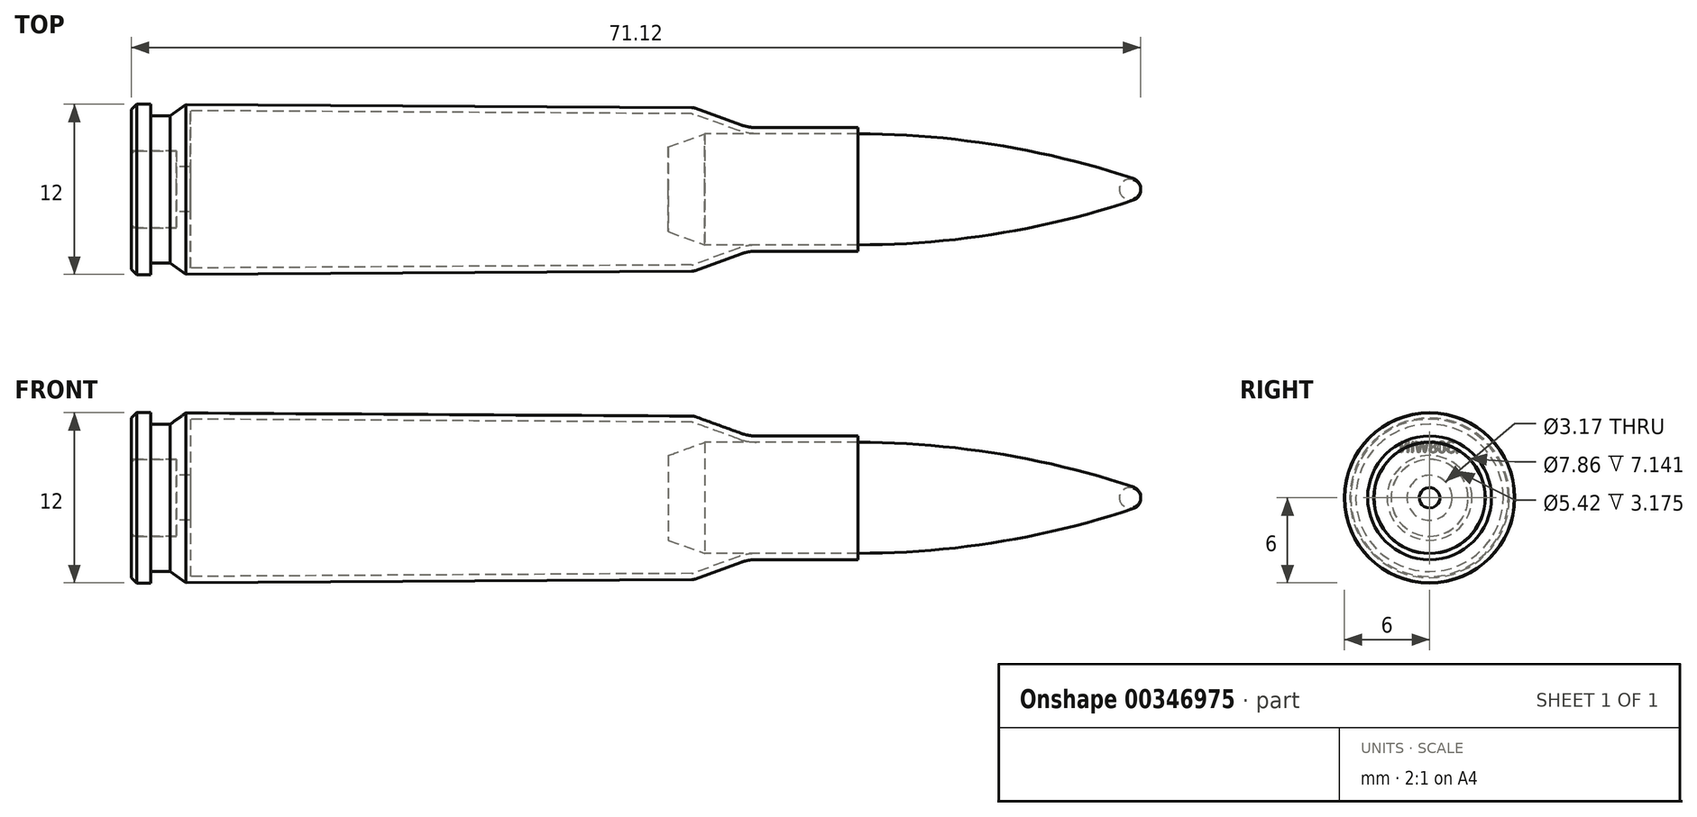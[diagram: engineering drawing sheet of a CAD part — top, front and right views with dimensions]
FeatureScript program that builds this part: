
annotation { "Feature Type Name" : "Feature", "Feature Type Description" : "" }
export const myFeature = defineFeature(function(context is Context, id is Id, definition is map)
    precondition{}
    {
        {
            var Q0;
            Q0=qCreatedBy(makeId("Front.planeOp"),FACE);
            var sketch = newSketch(context, id + "F0", { "sketchPlane" : qUnion([Q0])});
            skLineSegment(sketch, "E0", {"start": v(-35.56, 0) * mm, "end": v(35.56, 0) * mm});
            skPoint(sketch, "E1", {"position": v(0, 0) * mm});
            skLineSegment(sketch, "E2.top", {"start": v(-35.18, 6) * mm, "end": v(-34.2, 6) * mm});
            skLineSegment(sketch, "E2.left", {"start": v(-35.56, 0) * mm, "end": v(-35.56, 5.62) * mm});
            skLineSegment(sketch, "E3", {"start": v(4.18, 5.72) * mm, "end": v(7.4, 4.55) * mm});
            skLineSegment(sketch, "E4", {"start": v(8.48, 4.36) * mm, "end": v(15.62, 4.36) * mm});
            skLineSegment(sketch, "E5", {"start": v(15.62, 4.36) * mm, "end": v(15.62, 0) * mm});
            skArc(sketch, "E6", {"start": v(35.56, 0) * mm, "mid": v(35.43, 0.47) * mm, "end": v(35.04, 0.76) * mm});
            skLineSegment(sketch, "E7", {"start": v(4.83, 3.91) * mm, "end": v(15.62, 3.91) * mm});
            skArc(sketch, "E8", {"start": v(35.04, 0.76) * mm, "mid": v(25.46, 3.12) * mm, "end": v(15.62, 3.91) * mm});
            skLineSegment(sketch, "E9", {"start": v(2.29, 2.99) * mm, "end": v(2.29, 0) * mm});
            skLineSegment(sketch, "E10", {"start": v(-34.2, 6) * mm, "end": v(-34.2, 5.2) * mm});
            skLineSegment(sketch, "E11", {"start": v(-34.2, 5.2) * mm, "end": v(-32.8, 5.2) * mm});
            skLineSegment(sketch, "E12", {"start": v(-32.8, 5.2) * mm, "end": v(-31.7, 5.98) * mm});
            skLineSegment(sketch, "E13.trimOffspring", {"start": v(-31.7, 5.98) * mm, "end": v(3.93, 5.77) * mm});
            skPoint(sketch, "E14.visualSharp", {"position": v(4.06, 5.76) * mm});
            skArc(sketch, "E14.filletArc", {"start": v(4.18, 5.72) * mm, "mid": v(4.06, 5.75) * mm, "end": v(3.93, 5.77) * mm});
            skPoint(sketch, "E15.visualSharp", {"position": v(7.92, 4.36) * mm});
            skArc(sketch, "E15.filletArc", {"start": v(7.4, 4.55) * mm, "mid": v(7.93, 4.4) * mm, "end": v(8.48, 4.36) * mm});
            skLineSegment(sketch, "E16", {"start": v(-35.56, 5.62) * mm, "end": v(-35.18, 6) * mm});
            skLineSegment(sketch, "E17", {"start": v(2.29, 2.99) * mm, "end": v(4.83, 3.91) * mm});
            skSolve(sketch);
        }
        {
            var Q0;
            Q0=makeQuery(id+"F0.imprint","IMPRINT",FACE,{"disambiguationData":[TD([[makeQuery(id+"F0.imprint","IMPRINT",EDGE,{"derivedFrom":sQuery(id+"F0.wireOp",EDGE,"E2.top")}),-1.0]])]});
            var Q1;
            {var subQ3=sQuery(id+"F0.wireOp",EDGE,"E9");Q1=makeQuery(id+"F0.imprint","IMPRINT",FACE,{"disambiguationData":[TD([[makeQuery(id+"F0.imprint","IMPRINT",EDGE,{"derivedFrom":subQ3}),1.0]])]});}
            var Q2;
            Q2=sQuery(id+"F0.wireOp",EDGE,"E0");
            revolve(context, id + "F1", {"entities" : qUnion([Q0, Q1]), "axis" : qUnion([Q2]), "revolveType" : RevolveType.FULL});
        }
        {
            var Q0;
            {var subQ4=sQuery(id+"F0.wireOp",EDGE,"E6");Q0=makeQuery(id+"F0.imprint","IMPRINT",FACE,{"disambiguationData":[TD([[makeQuery(id+"F0.imprint","IMPRINT",EDGE,{"derivedFrom":subQ4}),1.0]])]});}
            var Q1;
            {var subQ3=sQuery(id+"F0.wireOp",EDGE,"E9");Q1=makeQuery(id+"F0.imprint","IMPRINT",FACE,{"disambiguationData":[TD([[makeQuery(id+"F0.imprint","IMPRINT",EDGE,{"derivedFrom":subQ3}),1.0]])]});}
            var Q2;
            Q2=sQuery(id+"F0.wireOp",EDGE,"E0");
            revolve(context, id + "F2", {"entities" : qUnion([Q0, Q1]), "axis" : qUnion([Q2]), "revolveType" : RevolveType.FULL});
        }
        {
            var Q0;
            Q0=makeQuery(id+"F1.opRevolve","SWEPT_FACE",FACE,{"disambiguationData":[OSD([sQuery(id+"F0.wireOp",EDGE,"E5")])]});
            shell(context, id + "F3", {"entities" : qUnion([Q0]), "thickness" : 0.43 * mm});
        }
        {
            var Q0;
            Q0=qCreatedBy(makeId("Front.planeOp"),FACE);
            var sketch = newSketch(context, id + "F4", { "sketchPlane" : qUnion([Q0])});
            skLineSegment(sketch, "E18.0", {"start": v(-35.56, 0) * mm, "end": v(-35.56, 5.62) * mm});
            skLineSegment(sketch, "E18.1", {"start": v(-35.56, 5.62) * mm, "end": v(-35.18, 6) * mm});
            skLineSegment(sketch, "E18.2", {"start": v(-35.18, 6) * mm, "end": v(-34.2, 6) * mm});
            skLineSegment(sketch, "E18.3", {"start": v(-34.2, 6) * mm, "end": v(-34.2, 5.2) * mm});
            skLineSegment(sketch, "E18.4", {"start": v(-34.2, 5.2) * mm, "end": v(-32.8, 5.2) * mm});
            skLineSegment(sketch, "E18.5", {"start": v(-32.8, 5.2) * mm, "end": v(-31.7, 5.98) * mm});
            skLineSegment(sketch, "E19", {"start": v(-31.7, 5.98) * mm, "end": v(-31.4, 5.98) * mm});
            skLineSegment(sketch, "E20", {"start": v(-35.56, 0) * mm, "end": v(-31.4, 0) * mm});
            skLineSegment(sketch, "E21", {"start": v(-31.4, 0) * mm, "end": v(-31.4, 5.98) * mm});
            skSolve(sketch);
        }
        {
            var Q0;
            Q0 = qSketchRegion(id + "F4", true);
            var Q1;
            Q1=sQuery(id+"F4.wireOp",EDGE,"E20");
            revolve(context, id + "F5", {"operationType" : NewBodyOperationType.ADD, "entities" : qUnion([Q0]), "axis" : qUnion([Q1]), "revolveType" : RevolveType.FULL});
        }
        {
            var Q0;
            Q0=makeQuery(id+"F1.opRevolve","SWEPT_FACE",FACE,{"disambiguationData":[OSD([sQuery(id+"F0.wireOp",EDGE,"E2.left")])]});
            var sketch = newSketch(context, id + "F6", { "sketchPlane" : qUnion([Q0])});
            skCircle(sketch, "E22", {"center": v(0, 0) * mm, "radius": 2.71 * mm});
            skCircle(sketch, "E23", {"center": v(0, 0) * mm, "radius": 1.59 * mm});
            skSolve(sketch);
        }
        {
            var Q0;
            Q0=makeQuery(id+"F6.imprint","IMPRINT",FACE,{"disambiguationData":[TD([[makeQuery(id+"F6.imprint","IMPRINT",EDGE,{"derivedFrom":sQuery(id+"F6.wireOp",EDGE,"E23")}),1.0]])]});
            extrude(context, id + "F7", {"entities" : qUnion([Q0]), "operationType" : NewBodyOperationType.REMOVE, "endBound" : BoundingType.UP_TO_NEXT, "oppositeDirection" : true, "depth" : 25.4 * mm});
        }
        {
            var Q0;
            Q0=makeQuery(id+"F6.imprint","IMPRINT",FACE,{"disambiguationData":[TD([[makeQuery(id+"F6.imprint","IMPRINT",EDGE,{"derivedFrom":sQuery(id+"F6.wireOp",EDGE,"E22")}),1.0]])]});
            var Q1;
            Q1=makeQuery(id+"F1.opRevolve","SWEPT_FACE",FACE,{"disambiguationData":[OSD([sQuery(id+"F0.wireOp",EDGE,"E10")])]});
            extrude(context, id + "F8", {"entities" : qUnion([Q0]), "operationType" : NewBodyOperationType.REMOVE, "oppositeDirection" : true, "endBoundEntityFace" : qUnion([Q1]), "depth" : 3.17 * mm});
        }
        {
            var Q0;
            Q0=qCreatedBy(makeId("Front.planeOp"),FACE);
            var sketch = newSketch(context, id + "F9", { "sketchPlane" : qUnion([Q0])});
            skLineSegment(sketch, "E24", {"start": v(-32.39, 0) * mm, "end": v(-35.56, 0) * mm});
            skLineSegment(sketch, "E25", {"start": v(-35.56, 0) * mm, "end": v(-35.56, 2.32) * mm});
            skLineSegment(sketch, "E26", {"start": v(-35.18, 2.7) * mm, "end": v(-32.39, 2.7) * mm});
            skLineSegment(sketch, "E27", {"start": v(-32.39, 2.7) * mm, "end": v(-32.39, 0) * mm});
            skPoint(sketch, "E28.visualSharp", {"position": v(-35.56, 2.7) * mm});
            skArc(sketch, "E28.filletArc", {"start": v(-35.18, 2.7) * mm, "mid": v(-35.45, 2.6) * mm, "end": v(-35.56, 2.32) * mm});
            skSolve(sketch);
        }
        {
            var Q0;
            Q0 = qSketchRegion(id + "F9", true);
            var Q1;
            Q1=sQuery(id+"F9.wireOp",EDGE,"E24");
            revolve(context, id + "F10", {"entities" : qUnion([Q0]), "axis" : qUnion([Q1]), "revolveType" : RevolveType.FULL});
        }
        {
            var Q0;
            Q0=makeQuery(id+"F1.opRevolve","SWEPT_FACE",FACE,{"disambiguationData":[OSD([sQuery(id+"F0.wireOp",EDGE,"E2.left")])]});
            var sketch = newSketch(context, id + "F11", { "sketchPlane" : qUnion([Q0])});
            skText(sketch, "E29", { "text": ".308WIN", "fontName": "NotoSansCJKjp-Regular.otf"});
            const initialGuessF11  = {"E29": [-0.0021, 0.00318, 1, 0, 0.0008]};
            skSetInitialGuess(sketch, initialGuessF11);
            skSolve(sketch);
        }
        {
            var Q0;
            Q0 = qSketchRegion(id + "F11", true);
            extrude(context, id + "F12", {"entities" : qUnion([Q0]), "operationType" : NewBodyOperationType.REMOVE, "oppositeDirection" : true, "depth" : 0.03 * mm});
        }
    });
